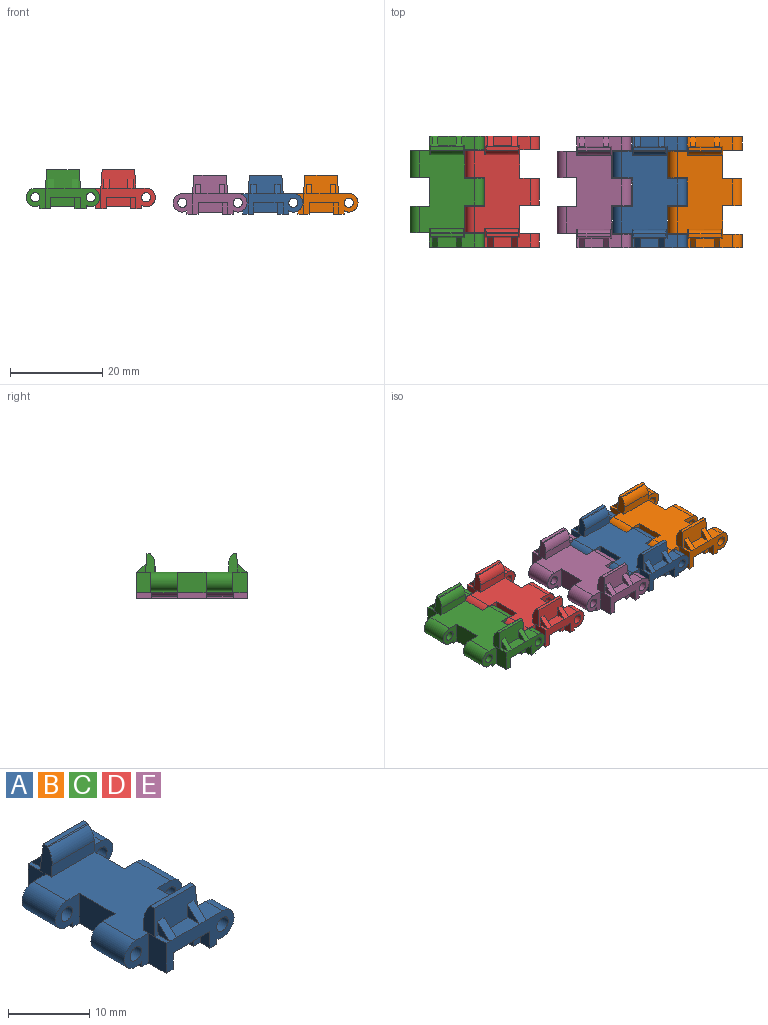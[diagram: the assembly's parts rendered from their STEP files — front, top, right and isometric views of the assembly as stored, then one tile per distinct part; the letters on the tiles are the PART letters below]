
ASSEMBLY  parts=5 mates=1
PART A: 96 faces, bbox 16x24x8.5 mm
  f0: plane 8.5x7.6mm, normal (0,0,-1), area 50.3mm2, adj f1,f2,f14,f39,f40,f45,f46,f47
  f1: plane 8.6x2.5mm, normal (-1,0,0), area 19.1mm2, adj f0,f13,f40,f41,f43,f50,f51,f52
  f2: plane 8.6x2.5mm, normal (1,0,0), area 16.7mm2, adj f0,f13,f45,f49,f50,f51,f52,f53
  f3: cylinder r=2mm len=5.8mm, axis (0,1,0), area 42.5mm2, adj f10,f18,f20,f44
  f4: cylinder r=2mm len=4mm, axis (0,1,0), area 21.3mm2, adj f7,f14,f16,f38
  f5: cylinder r=2mm len=5.8mm, axis (0,1,0), area 42.5mm2, adj f6,f10,f15,f36,f37,f57,f63,f83
  f6: plane 0.2x0mm, normal (0,0,-1), area 0mm2, adj f5,f15,f37
  f7: plane 2.9x2.8mm, normal (0,0,1), area 7.6mm2, adj f4,f14,f16,f27,f29,f31
  f8: plane 4x2mm, normal (0,0,1), area 8mm2, adj f14,f25,f28,f31
  f9: plane 2x0.6mm, normal (0,0,1), area 1.2mm2, adj f14,f21,f26,f31
  f10: plane 17.8x12mm, normal (0,0,1), area 159.9mm2, adj f3,f5,f15,f17,f18,f19,f20,f23
  f11: cylinder r=1mm len=2.9mm, axis (0,1,0), area 18.2mm2, adj f14,f16
  f12: cylinder r=1mm len=5.8mm, axis (0,1,0), area 36.4mm2, adj f15,f63
  f13: plane 6.4x4.6mm, normal (0,0,-1), area 28mm2, adj f1,f2,f41,f42,f51,f54,f87,f94
  f14: plane 11.8x4.5mm, normal (0,-1,0), area 30.7mm2, adj f0,f4,f7,f8,f9,f11,f21,f34
  f15: plane 4.2x4mm, normal (0,-1,0), area 10.7mm2, adj f5,f6,f10,f12,f17
  f16: plane 4.5x4.2mm, normal (0,1,0), area 12.5mm2, adj f4,f7,f11,f17,f38,f43
  f17: plane 6.2x4.5mm, normal (1,0,0), area 27.9mm2, adj f10,f15,f16,f29,f37,f43
  f18: plane 4.5x4.2mm, normal (0,1,0), area 12.5mm2, adj f3,f10,f19,f22,f44,f49
  f19: plane 6.2x4.5mm, normal (-1,0,0), area 27.9mm2, adj f10,f18,f49,f66
  f20: plane 4.5x4.2mm, normal (0,-1,0), area 12.5mm2, adj f3,f10,f21,f22,f44,f49
  f21: plane 4.5x3.1mm, normal (-1,0,0), area 14mm2, adj f9,f14,f20,f30,f49
  f22: cylinder r=1mm len=5.8mm, axis (0,1,0), area 36.4mm2, adj f18,f20
  f23: plane 7.6x1.76mm, normal (0,1,0), area 13.1mm2, adj f10,f29,f30,f33
  f24: plane 7x0.7mm, normal (0,0,1), area 4.9mm2, adj f29,f30,f31,f32
  f25: plane 2.15x1.95mm, normal (1,0,0), area 2mm2, adj f8,f31,f35
  f26: plane 2.15x1.95mm, normal (-1,0,0), area 2mm2, adj f9,f31,f35
  f27: plane 2.15x1.95mm, normal (1,0,0), area 2mm2, adj f7,f31,f34
  f28: plane 2.15x1.95mm, normal (-1,0,0), area 2mm2, adj f8,f31,f34
  f29: plane 4.01x2.01mm, normal (1,0,0.07), area 6.7mm2, adj f7,f17,f23,f24,f31,f32,f33
  f30: plane 4.01x2.01mm, normal (-1,0,0.07), area 6.7mm2, adj f10,f21,f23,f24,f31,f32,f33
  f31: plane 7.6x4mm, normal (0,-1,0.07), area 24.6mm2, adj f7,f8,f9,f24,f25,f26,f27,f28
  f32: plane 7.02x0.12mm, normal (0,0.71,0.71), area 1.2mm2, adj f24,f29,f30,f33
  f33: cylinder r=3mm len=7.34mm, axis (-1,0,0), area 16.9mm2, adj f23,f29,f30,f32
  f34: plane 2.15x1.95mm, normal (0,-0.67,0.74), area 3.5mm2, adj f14,f27,f28,f31
  f35: plane 2.15x1.95mm, normal (0,-0.67,0.74), area 3.5mm2, adj f14,f25,f26,f31
  f36: plane 5.78x0.77mm, normal (1,0,0), area 4.4mm2, adj f5,f37,f43,f83
  f37: plane 2.5x1.2mm, normal (0.01,-1,0), area 1.8mm2, adj f5,f6,f17,f36,f43
  f38: plane 2.9x0.77mm, normal (1,0,0), area 2.2mm2, adj f4,f14,f16,f43
  f39: plane 2.5x1.7mm, normal (-1,0,0), area 4.3mm2, adj f0,f14,f40,f43
  f40: plane 2.5x1.2mm, normal (0,-1,0), area 3mm2, adj f0,f1,f39,f43
  f41: plane 2.5x1.2mm, normal (0,1,0), area 3mm2, adj f1,f13,f42,f43
  f42: plane 3.4x2.5mm, normal (-1,0,0), area 8.5mm2, adj f13,f41,f43,f87
  f43: plane 24x2.4mm, normal (0,0,-1), area 34.5mm2, adj f1,f14,f16,f17,f36,f37,f38,f39
  f44: plane 5.8x0.77mm, normal (-1,0,0), area 4.5mm2, adj f3,f18,f20,f49
  f45: plane 2.5x1.2mm, normal (0,-1,0), area 3mm2, adj f0,f2,f46,f49
  f46: plane 3.4x2.5mm, normal (1,0,0), area 8.5mm2, adj f0,f45,f47,f49
  f47: plane 2.5x1.2mm, normal (0,1,0), area 3mm2, adj f0,f46,f48,f49
  f48: plane 4.3x2.5mm, normal (1,0,0), area 10.8mm2, adj f0,f14,f47,f49
  f49: plane 24x2.4mm, normal (0,0,-1), area 34.6mm2, adj f2,f14,f18,f19,f20,f21,f44,f45
  f50: plane 5.2x2mm, normal (0,-1,0), area 10.4mm2, adj f0,f1,f2,f52
  f51: plane 5.2x2mm, normal (0,1,0), area 10.4mm2, adj f1,f2,f13,f52
  f52: plane 5.2x1.2mm, normal (0,0,-1), area 6.2mm2, adj f1,f2,f50,f51
  f53: plane 8.5x7.6mm, normal (0,0,-1), area 50.3mm2, adj f2,f54,f62,f85,f86,f89,f90,f91
  f54: plane 8.6x2.5mm, normal (-1,0,0), area 19.1mm2, adj f13,f43,f53,f86,f87,f93,f94,f95
  f55: cylinder r=2mm len=5.8mm, axis (0,-1,0), area 42.5mm2, adj f10,f66,f67,f88
  f56: cylinder r=2mm len=4mm, axis (0,-1,0), area 21.3mm2, adj f58,f62,f64,f84
  f57: plane 0.2x0mm, normal (0,0,-1), area 0mm2, adj f5,f63,f83
  f58: plane 2.9x2.8mm, normal (0,0,1), area 7.6mm2, adj f56,f62,f64,f74,f76,f78
  f59: plane 4x2mm, normal (0,0,1), area 8mm2, adj f62,f72,f75,f78
  f60: plane 2x0.6mm, normal (0,0,1), area 1.2mm2, adj f62,f68,f73,f78
  f61: cylinder r=1mm len=2.9mm, axis (0,-1,0), area 18.2mm2, adj f62,f64
  f62: plane 11.8x4.5mm, normal (0,1,0), area 30.7mm2, adj f43,f49,f53,f56,f58,f59,f60,f61
  f63: plane 4.2x4mm, normal (0,1,0), area 10.7mm2, adj f5,f10,f12,f57,f65
  f64: plane 4.5x4.2mm, normal (0,-1,0), area 12.5mm2, adj f43,f56,f58,f61,f65,f84
  f65: plane 6.2x4.5mm, normal (1,0,0), area 27.9mm2, adj f10,f43,f63,f64,f76,f83
  f66: plane 4.5x4.2mm, normal (0,-1,0), area 12.5mm2, adj f10,f19,f49,f55,f69,f88
  f67: plane 4.5x4.2mm, normal (0,1,0), area 12.5mm2, adj f10,f49,f55,f68,f69,f88
  f68: plane 4.5x3.1mm, normal (-1,0,0), area 14mm2, adj f49,f60,f62,f67,f77
  f69: cylinder r=1mm len=5.8mm, axis (0,-1,0), area 36.4mm2, adj f66,f67
  f70: plane 7.6x1.76mm, normal (0,-1,0), area 13.1mm2, adj f10,f76,f77,f80
  f71: plane 7x0.7mm, normal (0,0,1), area 4.9mm2, adj f76,f77,f78,f79
  f72: plane 2.15x1.95mm, normal (1,0,0), area 2mm2, adj f59,f78,f82
  f73: plane 2.15x1.95mm, normal (-1,0,0), area 2mm2, adj f60,f78,f82
  f74: plane 2.15x1.95mm, normal (1,0,0), area 2mm2, adj f58,f78,f81
  f75: plane 2.15x1.95mm, normal (-1,0,0), area 2mm2, adj f59,f78,f81
  f76: plane 4.01x2.01mm, normal (1,0,0.07), area 6.7mm2, adj f58,f65,f70,f71,f78,f79,f80
  f77: plane 4.01x2.01mm, normal (-1,0,0.07), area 6.7mm2, adj f10,f68,f70,f71,f78,f79,f80
  f78: plane 7.6x4mm, normal (0,1,0.07), area 24.6mm2, adj f58,f59,f60,f71,f72,f73,f74,f75
  f79: plane 7.02x0.12mm, normal (0,-0.71,0.71), area 1.2mm2, adj f71,f76,f77,f80
  f80: cylinder r=3mm len=7.34mm, axis (-1,0,0), area 16.9mm2, adj f70,f76,f77,f79
  f81: plane 2.15x1.95mm, normal (0,0.67,0.74), area 3.5mm2, adj f62,f74,f75,f78
  f82: plane 2.15x1.95mm, normal (0,0.67,0.74), area 3.5mm2, adj f62,f72,f73,f78
  f83: plane 2.5x1.2mm, normal (0.01,1,0), area 1.8mm2, adj f5,f36,f43,f57,f65
  f84: plane 2.9x0.77mm, normal (1,0,0), area 2.2mm2, adj f43,f56,f62,f64
  f85: plane 2.5x1.7mm, normal (-1,0,0), area 4.3mm2, adj f43,f53,f62,f86
  f86: plane 2.5x1.2mm, normal (0,1,0), area 3mm2, adj f43,f53,f54,f85
  f87: plane 2.5x1.2mm, normal (0,-1,0), area 3mm2, adj f13,f42,f43,f54
  f88: plane 5.8x0.77mm, normal (-1,0,0), area 4.5mm2, adj f49,f55,f66,f67
  f89: plane 2.5x1.2mm, normal (0,1,0), area 3mm2, adj f2,f49,f53,f90
  f90: plane 3.4x2.5mm, normal (1,0,0), area 8.5mm2, adj f49,f53,f89,f91
  f91: plane 2.5x1.2mm, normal (0,-1,0), area 3mm2, adj f49,f53,f90,f92
  f92: plane 4.3x2.5mm, normal (1,0,0), area 10.8mm2, adj f49,f53,f62,f91
  f93: plane 5.2x2mm, normal (0,1,0), area 10.4mm2, adj f2,f53,f54,f95
  f94: plane 5.2x2mm, normal (0,-1,0), area 10.4mm2, adj f2,f13,f54,f95
  f95: plane 5.2x1.2mm, normal (0,0,-1), area 6.2mm2, adj f2,f54,f93,f94
PART B: same geometry as A
PART C: same geometry as A
PART D: same geometry as A
PART E: same geometry as A
PLACE A t=(24.03,-0.05,0)mm
PLACE B t=(36.03,-0.05,0)mm
PLACE C t=(-19.84,0.06,1.18)mm
PLACE D t=(-7.84,0.06,1.18)mm
PLACE E t=(12.01,-0.05,-0.01)mm
MATE revolute D.f22 <-> C.f11  axis (0,-1,0) through (-13.84,-8.84,1.18)mm
